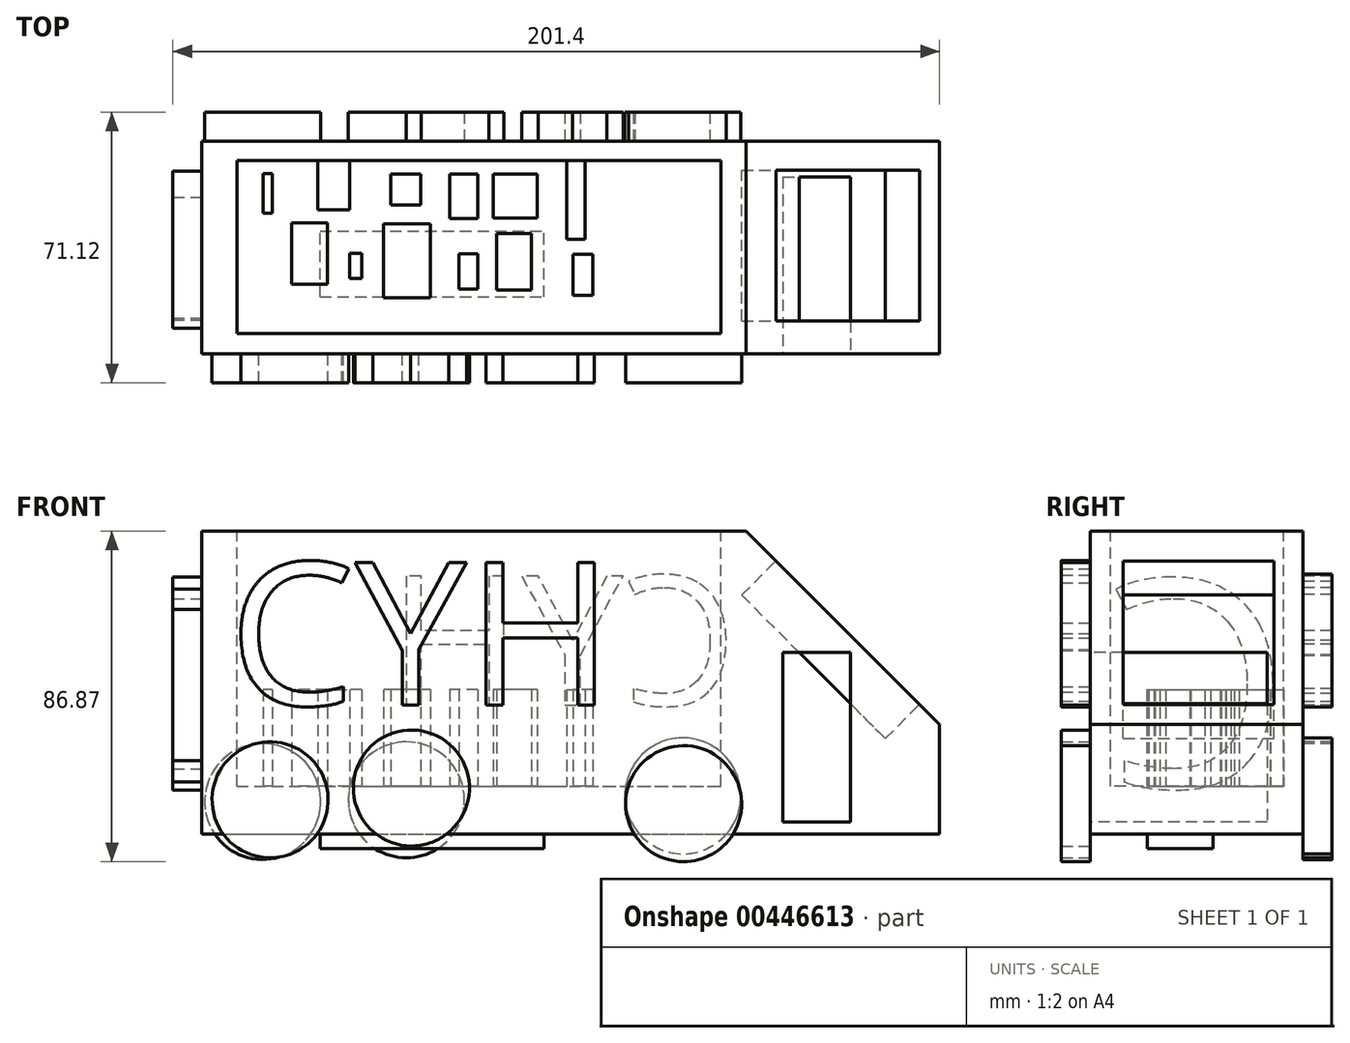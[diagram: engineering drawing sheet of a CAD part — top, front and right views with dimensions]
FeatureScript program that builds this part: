
annotation { "Feature Type Name" : "Feature", "Feature Type Description" : "" }
export const myFeature = defineFeature(function(context is Context, id is Id, definition is map)
    precondition{}
    {
        {
            var Q0;
            Q0=qCreatedBy(makeId("Front.planeOp"),FACE);
            var sketch = newSketch(context, id + "F0", { "sketchPlane" : qUnion([Q0])});
            skLineSegment(sketch, "E0.bottom", {"start": v(-72.53, 45.69) * mm, "end": v(121.25, 45.69) * mm});
            skLineSegment(sketch, "E0.top", {"start": v(-72.53, -33.95) * mm, "end": v(121.25, -33.95) * mm});
            skLineSegment(sketch, "E0.left", {"start": v(-72.53, 45.69) * mm, "end": v(-72.53, -33.95) * mm});
            skLineSegment(sketch, "E0.right", {"start": v(121.25, 45.69) * mm, "end": v(121.25, -33.95) * mm});
            skSolve(sketch);
        }
        {
            var Q0;
            Q0 = qSketchRegion(id + "F0", true);
            extrude(context, id + "F1", {"entities" : qUnion([Q0]), "depth" : 55.88 * mm, "offsetDistance" : 25.4 * mm});
        }
        {
            var Q0;
            Q0=makeQuery(id+"F1.opExtrude","SWEPT_EDGE",EDGE,{"disambiguationData":[OSD([sQuery(id+"F0.wireOp",EDGE,"E0.bottom"),sQuery(id+"F0.wireOp",EDGE,"E0.right")])]});
            chamfer(context, id + "F2", {"entities" : qUnion([Q0]), "width" : 50.8 * mm, "tangentPropagation" : true});
        }
        {
            var Q0;
            Q0=makeQuery(id+"F1.opExtrude","CAP_FACE",FACE,{"disambiguationData":[OSD([sQuery(id+"F0.wireOp",EDGE,"E0.bottom"),sQuery(id+"F0.wireOp",EDGE,"E0.top"),sQuery(id+"F0.wireOp",EDGE,"E0.left"),sQuery(id+"F0.wireOp",EDGE,"E0.right")])],"isStart":false});
            var sketch = newSketch(context, id + "F3", { "sketchPlane" : qUnion([Q0])});
            skLineSegment(sketch, "E1.bottom", {"start": v(80.08, 13.78) * mm, "end": v(97.86, 13.78) * mm});
            skLineSegment(sketch, "E1.top", {"start": v(80.08, -30.73) * mm, "end": v(97.86, -30.73) * mm});
            skLineSegment(sketch, "E1.left", {"start": v(80.08, 13.78) * mm, "end": v(80.08, -30.73) * mm});
            skLineSegment(sketch, "E1.right", {"start": v(97.86, 13.78) * mm, "end": v(97.86, -30.73) * mm});
            skSolve(sketch);
        }
        {
            var Q0;
            Q0 = qSketchRegion(id + "F3", true);
            extrude(context, id + "F4", {"entities" : qUnion([Q0]), "operationType" : NewBodyOperationType.REMOVE, "oppositeDirection" : true, "depth" : 46.48 * mm, "offsetDistance" : 25.4 * mm});
        }
        {
            var Q0;
            Q0=makeQuery(id+"F2.opChamfer","BLEND_FACE",FACE,{"disambiguationData":[OSD([sQuery(id+"F0.wireOp",EDGE,"E0.bottom"),sQuery(id+"F0.wireOp",EDGE,"E0.right")])]});
            var sketch = newSketch(context, id + "F5", { "sketchPlane" : qUnion([Q0])});
            skLineSegment(sketch, "E2.bottom", {"start": v(-47.25, -28.57) * mm, "end": v(-7.67, -28.57) * mm});
            skLineSegment(sketch, "E2.top", {"start": v(-47.25, -81.91) * mm, "end": v(-7.67, -81.91) * mm});
            skLineSegment(sketch, "E2.left", {"start": v(-47.25, -28.57) * mm, "end": v(-47.25, -81.91) * mm});
            skLineSegment(sketch, "E2.right", {"start": v(-7.67, -28.57) * mm, "end": v(-7.67, -81.91) * mm});
            skSolve(sketch);
        }
        {
            var Q0;
            Q0 = qSketchRegion(id + "F5", true);
            extrude(context, id + "F6", {"entities" : qUnion([Q0]), "operationType" : NewBodyOperationType.REMOVE, "oppositeDirection" : true, "depth" : 12.7 * mm, "offsetDistance" : 25.4 * mm});
        }
        {
            var Q0;
            Q0=makeQuery(id+"F1.opExtrude","SWEPT_FACE",FACE,{"disambiguationData":[OSD([sQuery(id+"F0.wireOp",EDGE,"E0.bottom")])]});
            var sketch = newSketch(context, id + "F7", { "sketchPlane" : qUnion([Q0])});
            skLineSegment(sketch, "E3.bottom", {"start": v(-63.36, -5.1) * mm, "end": v(63.83, -5.1) * mm});
            skLineSegment(sketch, "E3.top", {"start": v(-63.36, -50.54) * mm, "end": v(63.83, -50.54) * mm});
            skLineSegment(sketch, "E3.left", {"start": v(-63.36, -5.1) * mm, "end": v(-63.36, -50.54) * mm});
            skLineSegment(sketch, "E3.right", {"start": v(63.83, -5.1) * mm, "end": v(63.83, -50.54) * mm});
            skSolve(sketch);
        }
        {
            var Q0;
            Q0 = qSketchRegion(id + "F7", true);
            extrude(context, id + "F8", {"entities" : qUnion([Q0]), "operationType" : NewBodyOperationType.REMOVE, "oppositeDirection" : true, "depth" : 67.06 * mm, "offsetDistance" : 25.4 * mm});
        }
        {
            var Q0;
            Q0=makeQuery(id+"F1.opExtrude","CAP_FACE",FACE,{"disambiguationData":[OSD([sQuery(id+"F0.wireOp",EDGE,"E0.bottom"),sQuery(id+"F0.wireOp",EDGE,"E0.top"),sQuery(id+"F0.wireOp",EDGE,"E0.left"),sQuery(id+"F0.wireOp",EDGE,"E0.right")])],"isStart":false});
            var sketch = newSketch(context, id + "F9", { "sketchPlane" : qUnion([Q0])});
            skCircle(sketch, "E4", {"center": v(-54.62, -24.91) * mm, "radius": 15.24 * mm});
            skCircle(sketch, "E5", {"center": v(54.01, -25.94) * mm, "radius": 15.24 * mm});
            skSolve(sketch);
        }
        {
            var Q0;
            Q0 = qSketchRegion(id + "F9", true);
            extrude(context, id + "F10", {"entities" : qUnion([Q0]), "operationType" : NewBodyOperationType.ADD, "depth" : 7.62 * mm, "offsetDistance" : 25.4 * mm});
        }
        {
            var Q0;
            Q0=makeQuery(id+"F1.opExtrude","CAP_FACE",FACE,{"disambiguationData":[OSD([sQuery(id+"F0.wireOp",EDGE,"E0.bottom"),sQuery(id+"F0.wireOp",EDGE,"E0.top"),sQuery(id+"F0.wireOp",EDGE,"E0.left"),sQuery(id+"F0.wireOp",EDGE,"E0.right")])],"isStart":true});
            var sketch = newSketch(context, id + "F11", { "sketchPlane" : qUnion([Q0])});
            skCircle(sketch, "E6", {"center": v(56.56, -25.38) * mm, "radius": 15.24 * mm});
            skCircle(sketch, "E7", {"center": v(-53.84, -23.87) * mm, "radius": 15.24 * mm});
            skSolve(sketch);
        }
        {
            var Q0;
            Q0 = qSketchRegion(id + "F11", true);
            extrude(context, id + "F12", {"entities" : qUnion([Q0]), "operationType" : NewBodyOperationType.ADD, "depth" : 7.62 * mm, "offsetDistance" : 25.4 * mm});
        }
        {
            var Q0;
            Q0=makeQuery(id+"F1.opExtrude","CAP_FACE",FACE,{"disambiguationData":[OSD([sQuery(id+"F0.wireOp",EDGE,"E0.bottom"),sQuery(id+"F0.wireOp",EDGE,"E0.top"),sQuery(id+"F0.wireOp",EDGE,"E0.left"),sQuery(id+"F0.wireOp",EDGE,"E0.right")])],"isStart":true});
            var sketch = newSketch(context, id + "F13", { "sketchPlane" : qUnion([Q0])});
            skCircle(sketch, "E8", {"center": v(18.82, -24.94) * mm, "radius": 15.24 * mm});
            skSolve(sketch);
        }
        {
            var Q0;
            Q0 = qSketchRegion(id + "F13", true);
            extrude(context, id + "F14", {"entities" : qUnion([Q0]), "operationType" : NewBodyOperationType.ADD, "depth" : 7.62 * mm, "offsetDistance" : 25.4 * mm});
        }
        {
            var Q0;
            Q0=makeQuery(id+"F1.opExtrude","CAP_FACE",FACE,{"disambiguationData":[OSD([sQuery(id+"F0.wireOp",EDGE,"E0.bottom"),sQuery(id+"F0.wireOp",EDGE,"E0.top"),sQuery(id+"F0.wireOp",EDGE,"E0.left"),sQuery(id+"F0.wireOp",EDGE,"E0.right")])],"isStart":false});
            var sketch = newSketch(context, id + "F15", { "sketchPlane" : qUnion([Q0])});
            skCircle(sketch, "E9", {"center": v(-17.5, -21.82) * mm, "radius": 15.24 * mm});
            skSolve(sketch);
        }
        {
            var Q0;
            Q0 = qSketchRegion(id + "F15", true);
            extrude(context, id + "F16", {"entities" : qUnion([Q0]), "operationType" : NewBodyOperationType.ADD, "depth" : 7.62 * mm, "offsetDistance" : 25.4 * mm});
        }
        {
            var Q0;
            Q0=makeQuery(id+"F1.opExtrude","CAP_FACE",FACE,{"disambiguationData":[OSD([sQuery(id+"F0.wireOp",EDGE,"E0.bottom"),sQuery(id+"F0.wireOp",EDGE,"E0.top"),sQuery(id+"F0.wireOp",EDGE,"E0.left"),sQuery(id+"F0.wireOp",EDGE,"E0.right")])],"isStart":true});
            var sketch = newSketch(context, id + "F17", { "sketchPlane" : qUnion([Q0])});
            skText(sketch, "E10", { "text": "CYH   ", "fontName": "OpenSans-Regular.ttf"});
            const initialGuessF17  = {"E10": [-0.06808, 0, 1, 0, 0.0342]};
            skSetInitialGuess(sketch, initialGuessF17);
            skSolve(sketch);
        }
        {
            var Q0;
            Q0 = qSketchRegion(id + "F17", true);
            extrude(context, id + "F18", {"entities" : qUnion([Q0]), "operationType" : NewBodyOperationType.ADD, "depth" : 7.62 * mm, "offsetDistance" : 25.4 * mm});
        }
        {
            var Q0;
            Q0=makeQuery(id+"F1.opExtrude","CAP_FACE",FACE,{"disambiguationData":[OSD([sQuery(id+"F0.wireOp",EDGE,"E0.bottom"),sQuery(id+"F0.wireOp",EDGE,"E0.top"),sQuery(id+"F0.wireOp",EDGE,"E0.left"),sQuery(id+"F0.wireOp",EDGE,"E0.right")])],"isStart":false});
            var sketch = newSketch(context, id + "F19", { "sketchPlane" : qUnion([Q0])});
            skText(sketch, "E11", { "text": "CYH", "fontName": "OpenSans-Regular.ttf"});
            const initialGuessF19  = {"E11": [-0.06548, 0, 1, 0, 0.03778]};
            skSetInitialGuess(sketch, initialGuessF19);
            skSolve(sketch);
        }
        {
            var Q0;
            Q0 = qSketchRegion(id + "F19", true);
            extrude(context, id + "F20", {"entities" : qUnion([Q0]), "operationType" : NewBodyOperationType.ADD, "depth" : 7.62 * mm, "offsetDistance" : 25.4 * mm});
        }
        {
            var Q0;
            Q0=makeQuery(id+"F1.opExtrude","SWEPT_FACE",FACE,{"disambiguationData":[OSD([sQuery(id+"F0.wireOp",EDGE,"E0.left")])]});
            var sketch = newSketch(context, id + "F21", { "sketchPlane" : qUnion([Q0])});
            skText(sketch, "E12", { "text": "C", "fontName": "OpenSans-Regular.ttf"});
            const initialGuessF21  = {"E12": [0.00326, -0.0216, 1, 0, 0.05492]};
            skSetInitialGuess(sketch, initialGuessF21);
            skSolve(sketch);
        }
        {
            var Q0;
            Q0 = qSketchRegion(id + "F21", true);
            extrude(context, id + "F22", {"entities" : qUnion([Q0]), "operationType" : NewBodyOperationType.ADD, "depth" : 7.62 * mm, "offsetDistance" : 25.4 * mm});
        }
        {
            var Q0;
            Q0=makeQuery(id+"F1.opExtrude","SWEPT_FACE",FACE,{"disambiguationData":[OSD([sQuery(id+"F0.wireOp",EDGE,"E0.top")])]});
            var sketch = newSketch(context, id + "F23", { "sketchPlane" : qUnion([Q0])});
            skLineSegment(sketch, "E13.bottom", {"start": v(-41.5, 40.95) * mm, "end": v(17.4, 40.95) * mm});
            skLineSegment(sketch, "E13.top", {"start": v(-41.5, 23.63) * mm, "end": v(17.4, 23.63) * mm});
            skLineSegment(sketch, "E13.left", {"start": v(-41.5, 40.95) * mm, "end": v(-41.5, 23.63) * mm});
            skLineSegment(sketch, "E13.right", {"start": v(17.4, 40.95) * mm, "end": v(17.4, 23.63) * mm});
            skSolve(sketch);
        }
        {
            var Q0;
            Q0 = qSketchRegion(id + "F23", true);
            extrude(context, id + "F24", {"entities" : qUnion([Q0]), "operationType" : NewBodyOperationType.ADD, "depth" : 3.8 * mm, "offsetDistance" : 25.4 * mm});
        }
        {
            var Q0;
            Q0=makeQuery(id+"F8.boolean.opBoolean","COPY",FACE,{"derivedFrom":makeQuery(id+"F8.opExtrude","CAP_FACE",FACE,{"disambiguationData":[OSD([sQuery(id+"F7.wireOp",EDGE,"E3.bottom"),sQuery(id+"F7.wireOp",EDGE,"E3.top"),sQuery(id+"F7.wireOp",EDGE,"E3.left"),sQuery(id+"F7.wireOp",EDGE,"E3.right")])],"isStart":false})});
            var sketch = newSketch(context, id + "F25", { "sketchPlane" : qUnion([Q0])});
            skLineSegment(sketch, "E14.bottom", {"start": v(30.2, -40.52) * mm, "end": v(24.94, -40.52) * mm});
            skLineSegment(sketch, "E14.top", {"start": v(30.2, -29.78) * mm, "end": v(24.94, -29.78) * mm});
            skLineSegment(sketch, "E14.left", {"start": v(30.2, -40.52) * mm, "end": v(30.2, -29.78) * mm});
            skLineSegment(sketch, "E14.right", {"start": v(24.94, -40.52) * mm, "end": v(24.94, -29.78) * mm});
            skLineSegment(sketch, "E15.bottom", {"start": v(14.06, -39.1) * mm, "end": v(4.9, -39.1) * mm});
            skLineSegment(sketch, "E15.top", {"start": v(14.06, -24.3) * mm, "end": v(4.9, -24.3) * mm});
            skLineSegment(sketch, "E15.left", {"start": v(14.06, -39.1) * mm, "end": v(14.06, -24.3) * mm});
            skLineSegment(sketch, "E15.right", {"start": v(4.9, -39.1) * mm, "end": v(4.9, -24.3) * mm});
            skLineSegment(sketch, "E16.bottom", {"start": v(28.08, -25.8) * mm, "end": v(23.32, -25.8) * mm});
            skLineSegment(sketch, "E16.top", {"start": v(28.08, -5.1) * mm, "end": v(23.32, -5.1) * mm});
            skLineSegment(sketch, "E16.left", {"start": v(28.08, -25.8) * mm, "end": v(28.08, -5.1) * mm});
            skLineSegment(sketch, "E16.right", {"start": v(23.32, -25.8) * mm, "end": v(23.32, -5.1) * mm});
            skLineSegment(sketch, "E17.bottom", {"start": v(-12.47, -41.1) * mm, "end": v(-24.83, -41.1) * mm});
            skLineSegment(sketch, "E17.top", {"start": v(-12.47, -21.7) * mm, "end": v(-24.83, -21.7) * mm});
            skLineSegment(sketch, "E17.left", {"start": v(-12.47, -41.1) * mm, "end": v(-12.47, -21.7) * mm});
            skLineSegment(sketch, "E17.right", {"start": v(-24.83, -41.1) * mm, "end": v(-24.83, -21.7) * mm});
            skLineSegment(sketch, "E18.bottom", {"start": v(-39.57, -37.56) * mm, "end": v(-49, -37.56) * mm});
            skLineSegment(sketch, "E18.top", {"start": v(-39.57, -21.42) * mm, "end": v(-49, -21.42) * mm});
            skLineSegment(sketch, "E18.left", {"start": v(-39.57, -37.56) * mm, "end": v(-39.57, -21.42) * mm});
            skLineSegment(sketch, "E18.right", {"start": v(-49, -37.56) * mm, "end": v(-49, -21.42) * mm});
            skLineSegment(sketch, "E19.bottom", {"start": v(0, -20.3) * mm, "end": v(-7.37, -20.3) * mm});
            skLineSegment(sketch, "E19.top", {"start": v(0, -8.6) * mm, "end": v(-7.37, -8.6) * mm});
            skLineSegment(sketch, "E19.left", {"start": v(0, -20.3) * mm, "end": v(0, -8.6) * mm});
            skLineSegment(sketch, "E19.right", {"start": v(-7.37, -20.3) * mm, "end": v(-7.37, -8.6) * mm});
            skLineSegment(sketch, "E20.bottom", {"start": v(-33.74, -18) * mm, "end": v(-42.13, -18) * mm});
            skLineSegment(sketch, "E20.top", {"start": v(-33.74, -5.1) * mm, "end": v(-42.13, -5.1) * mm});
            skLineSegment(sketch, "E20.left", {"start": v(-33.74, -18) * mm, "end": v(-33.74, -5.1) * mm});
            skLineSegment(sketch, "E20.right", {"start": v(-42.13, -18) * mm, "end": v(-42.13, -5.1) * mm});
            skLineSegment(sketch, "E21.bottom", {"start": v(-54.04, -18.91) * mm, "end": v(-56.39, -18.91) * mm});
            skLineSegment(sketch, "E21.top", {"start": v(-54.04, -8.57) * mm, "end": v(-56.39, -8.57) * mm});
            skLineSegment(sketch, "E21.left", {"start": v(-54.04, -18.91) * mm, "end": v(-54.04, -8.57) * mm});
            skLineSegment(sketch, "E21.right", {"start": v(-56.39, -18.91) * mm, "end": v(-56.39, -8.57) * mm});
            skLineSegment(sketch, "E22.bottom", {"start": v(-15.08, -16.8) * mm, "end": v(-22.86, -16.8) * mm});
            skLineSegment(sketch, "E22.top", {"start": v(-15.08, -8.67) * mm, "end": v(-22.86, -8.67) * mm});
            skLineSegment(sketch, "E22.left", {"start": v(-15.08, -16.8) * mm, "end": v(-15.08, -8.67) * mm});
            skLineSegment(sketch, "E22.right", {"start": v(-22.86, -16.8) * mm, "end": v(-22.86, -8.67) * mm});
            skLineSegment(sketch, "E23.bottom", {"start": v(15.61, -20.2) * mm, "end": v(4, -20.2) * mm});
            skLineSegment(sketch, "E23.top", {"start": v(15.61, -8.6) * mm, "end": v(4, -8.6) * mm});
            skLineSegment(sketch, "E23.left", {"start": v(15.61, -20.2) * mm, "end": v(15.61, -8.6) * mm});
            skLineSegment(sketch, "E23.right", {"start": v(4, -20.2) * mm, "end": v(4, -8.6) * mm});
            skLineSegment(sketch, "E24.bottom", {"start": v(0, -38.86) * mm, "end": v(-5, -38.86) * mm});
            skLineSegment(sketch, "E24.top", {"start": v(0, -29.54) * mm, "end": v(-5, -29.54) * mm});
            skLineSegment(sketch, "E24.left", {"start": v(0, -38.86) * mm, "end": v(0, -29.54) * mm});
            skLineSegment(sketch, "E24.right", {"start": v(-5, -38.86) * mm, "end": v(-5, -29.54) * mm});
            skLineSegment(sketch, "E25.bottom", {"start": v(-30.49, -36.04) * mm, "end": v(-33.66, -36.04) * mm});
            skLineSegment(sketch, "E25.top", {"start": v(-30.49, -29.43) * mm, "end": v(-33.66, -29.43) * mm});
            skLineSegment(sketch, "E25.left", {"start": v(-30.49, -36.04) * mm, "end": v(-30.49, -29.43) * mm});
            skLineSegment(sketch, "E25.right", {"start": v(-33.66, -36.04) * mm, "end": v(-33.66, -29.43) * mm});
            skSolve(sketch);
        }
        {
            var Q0;
            Q0 = qSketchRegion(id + "F25", true);
            extrude(context, id + "F26", {"entities" : qUnion([Q0]), "operationType" : NewBodyOperationType.ADD, "depth" : 25.4 * mm, "offsetDistance" : 25.4 * mm});
        }
    });
